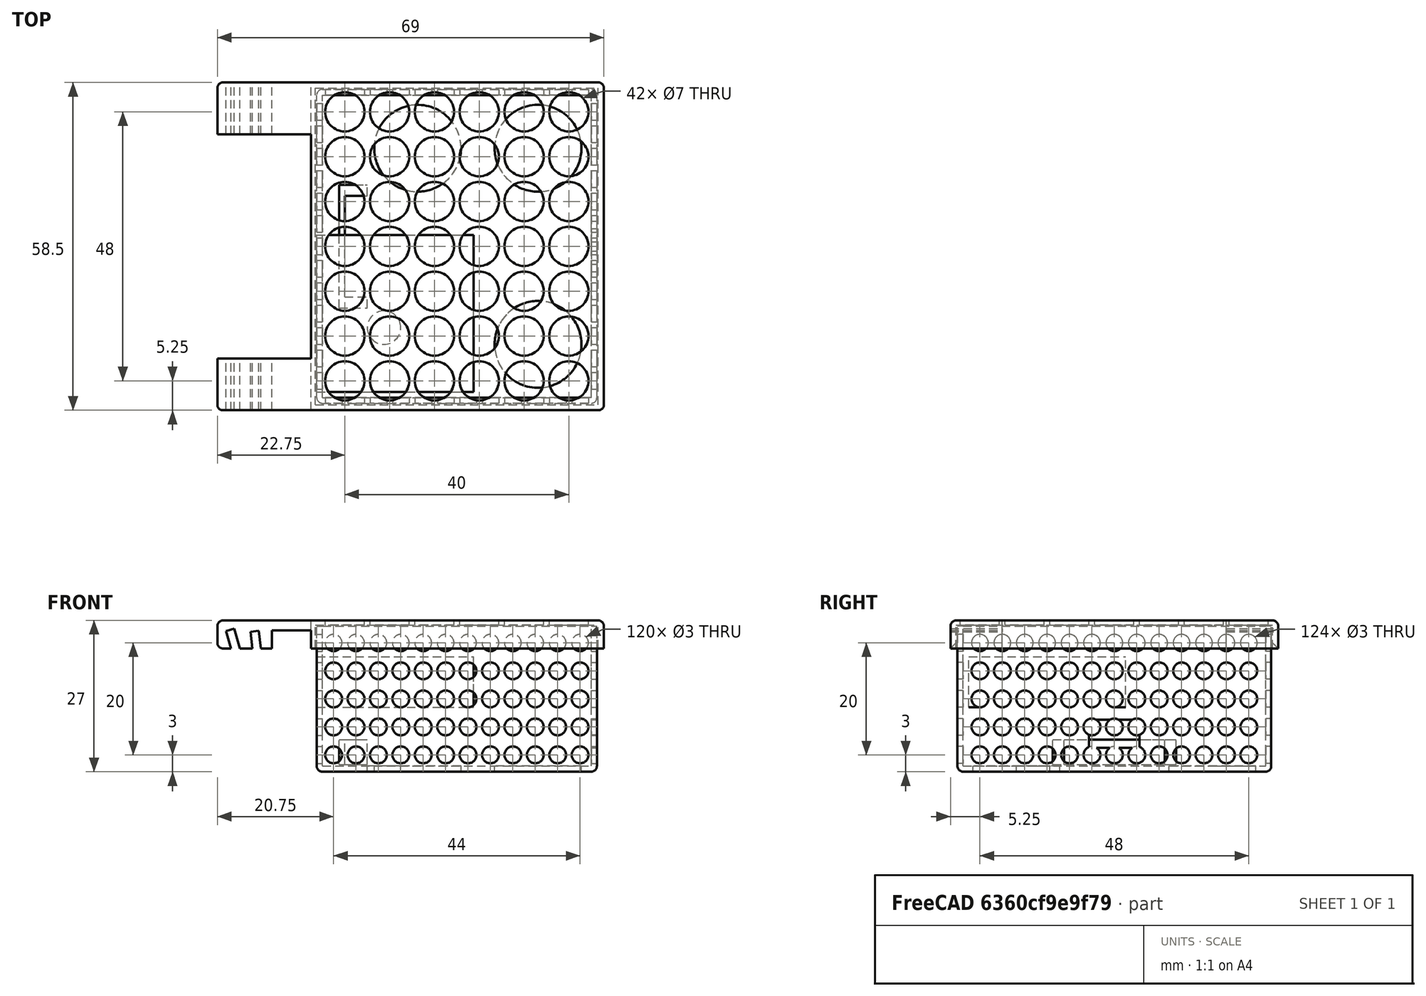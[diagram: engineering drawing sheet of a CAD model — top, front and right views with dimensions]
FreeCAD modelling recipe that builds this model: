
FCSTD DOCUMENT  (FreeCAD 0.16R6703 (Git))
Label: Electronics_BOX_v23
Comment: Muy grande, hay que reducir.. 0,5mm el ancho y largo, \nreducir la base a 0,8mm \naumentar el largo del soporte cortando el 80% desde el centro\naumentar el radio de los agujeros.?
License: CreativeCommons Attribution-ShareAlike
LicenseURL: http://creativecommons.org/licenses/by-sa/4.0/
objects: Part::Box×12, Part::Cut×9, Part::Cylinder×7, Part::MultiFuse×5, Part::FeaturePython×3, Part::Fillet×2
note: 38 computed .brp shape members not serialized (recipe doc carries the construction recipe); baked Part::Feature solids carry a one-line shape summary decoded from their .brp

FEATURE [Part::Box] Box  label="dummy arduino"
  Height = 4.5
  Length = 44
  Placement = pos=(-20,-9,-11.75) rot=(0,0,1;0rad)
  Width = 18
FEATURE [Part::Cylinder] Cylinder  label="Dummy_Button"
  Angle = 360
  Height = 21
  Placement = pos=(14.5,-17.5,-13.5) rot=(0,0,1;0rad)
  Radius = 7.75
FEATURE [Part::Box] Box001  label="dummy RTC"
  Height = 9
  Length = 28
  Placement = pos=(-25,-26,-1.5) rot=(0,0,1;0rad)
  Width = 28
FEATURE [Part::Box] Box002  label="box_int"
  Height = 28
  Length = 48
  Placement = pos=(-24,-27,-12) rot=(0,0,1;0rad)
  Width = 54
FEATURE [Part::Box] Box003  label="box_ext"
  Height = 26
  Length = 50
  Placement = pos=(-25,-28,-13) rot=(0,0,1;0rad)
  Width = 56
FEATURE [Part::Cut] Cut  label="Box"
  Base = -> Box003
  Tool = -> Box002
FEATURE [Part::Box] Box004  label="dummy arduino_usb"
  Height = 5
  Length = 44
  Placement = pos=(-13,-4.5,-8.75) rot=(0,0,1;0rad)
  Width = 9
FEATURE [Part::MultiFuse] Fusion  label="dummy_ardu"
  Shapes = -> [Box,Box004]
FEATURE [Part::Box] Box005  label="soporte_top_arduino"
  Height = 4.5
  Length = 5
  Placement = pos=(-21,-11,-11.75) rot=(0,0,1;0rad)
  Width = 22
FEATURE [Part::Cylinder] Cylinder001  label="Dummy_Button001"
  Angle = 360
  Height = 21
  Placement = pos=(-7,17.5,-13.5) rot=(0,0,1;0rad)
  Radius = 7.75
FEATURE [Part::Cylinder] Cylinder002  label="Dummy_Button002"
  Angle = 360
  Height = 21
  Placement = pos=(14.5,17.5,-13.5) rot=(0,0,1;0rad)
  Radius = 7.75
FEATURE [Part::Cylinder] Cylinder003  label="Hole"
  Angle = 360
  Height = 6
  Placement = pos=(-13,-14.5,-15.5) rot=(0,0,1;0rad)
  Radius = 3
FEATURE [Part::MultiFuse] Fusion001  label="buttons_hole"
  Shapes = -> [Cylinder002,Cylinder001,Cylinder,Cylinder003]
FEATURE [Part::Cylinder] Cylinder004  label="Cylinder"
  Angle = 360
  Height = 90
  Placement = pos=(22,45,10) rot=(1,0,0;1.5708rad)
  Radius = 1.5
FEATURE [Part::FeaturePython] Array  # Draft array (typed FeaturePython)
  Angle = 360
  ArrayType = 0
  Axis = (0,0,1)
  Base = -> Cylinder004
  Center = (0,0,0)
  Fuse = false
  IntervalAxis = (0,0,0)
  IntervalX = (-4,0,0)
  IntervalY = (0,3,0)
  IntervalZ = (0,0,-5)
  NumberPolar = 1
  NumberX = 12
  NumberY = 1
  NumberZ = 5
FEATURE [Part::Cylinder] Cylinder005  label="Cylinder001"
  Angle = 360
  Height = 90
  Placement = pos=(-42,-24,-10) rot=(0,1,0;1.5708rad)
  Radius = 1.5
FEATURE [Part::FeaturePython] Array001  # Draft array (typed FeaturePython)
  Angle = 360
  ArrayType = 0
  Axis = (0,0,1)
  Base = -> Cylinder005
  Center = (0,0,0)
  Fuse = false
  IntervalAxis = (0,0,0)
  IntervalX = (4,0,0)
  IntervalY = (0,4,0)
  IntervalZ = (0,0,5)
  NumberPolar = 1
  NumberX = 1
  NumberY = 13
  NumberZ = 5
FEATURE [Part::MultiFuse] Fusion002  label="holes"
  Shapes = -> [Array,Array001]
FEATURE [Part::Cut] Cut001  label="box_w_holes"
  Base = -> Cut
  Tool = -> Fusion002
FEATURE [Part::MultiFuse] Fusion003
  Shapes = -> [Cut001,Box005]
FEATURE [Part::Cut] Cut002
  Base = -> Fusion003
  Tool = -> Fusion
FEATURE [Part::Cut] Cut003
  Base = -> Cut002
  Tool = -> Fusion001
FEATURE [Part::Fillet] Fillet
  Base = -> Cut003
  Edges = 8 edges r=1: [Edge25,Edge27,Edge28,Edge94,Edge95,Edge163,Edge164,Edge169]
FEATURE [Part::Box] Box006  label="box_int001"
  Height = 4.2
  Length = 50.5
  Placement = pos=(-25.25,-28.25,9) rot=(0,0,1;0rad)
  Width = 56.5
FEATURE [Part::Box] Box007  label="box_ext_001"
  Height = 5
  Length = 69
  Placement = pos=(-42.75,-29.25,9) rot=(0,0,1;0rad)
  Width = 58.5
FEATURE [Part::Cut] Cut004
  Base = -> Box007
  Tool = -> Box006
FEATURE [Part::Box] Box008  label="Cube"
  Height = 72.5
  Length = 1.5
  Placement = pos=(-28,-50,-60) rot=(0,-1,0;0.122173rad)
  Width = 100
FEATURE [Part::Box] Box009  label="Cube001"
  Height = 75
  Length = 1.5
  Placement = pos=(-20.5,-50,-60) rot=(0,-1,0;0.279253rad)
  Width = 100
FEATURE [Part::MultiFuse] Fusion004
  Shapes = -> [Box008,Box009]
FEATURE [Part::Cut] Cut005
  Base = -> Cut004
  Tool = -> Fusion004
FEATURE [Part::Cylinder] Cylinder006  label="Cylinder002"
  Angle = 360
  Height = 8
  Placement = pos=(-20,24,10) rot=(0,0,1;0rad)
  Radius = 3.5
FEATURE [Part::FeaturePython] Array002  # Draft array (typed FeaturePython)
  Angle = 360
  ArrayType = 0
  Axis = (0,0,1)
  Base = -> Cylinder006
  Center = (0,0,0)
  Fuse = false
  IntervalAxis = (0,0,0)
  IntervalX = (8,0,0)
  IntervalY = (0,-8,0)
  IntervalZ = (0,0,0)
  NumberPolar = 1
  NumberX = 6
  NumberY = 7
  NumberZ = 1
FEATURE [Part::Cut] Cut006
  Base = -> Cut005
  Tool = -> Array002
FEATURE [Part::Fillet] Fillet001
  Base = -> Cut006
  Edges = 9 edges r=1: [Edge1,Edge2,Edge3,Edge4,Edge14,Edge15,Edge16,Edge17,Edge69]
FEATURE [Part::Box] Box010  label="Cube002"
  Height = 72.25
  Length = 7
  Placement = pos=(-33,-50,-60) rot=(0,0,1;0rad)
  Width = 100
FEATURE [Part::Cut] Cut007
  Base = -> Fillet001
  Tool = -> Box010
FEATURE [Part::Box] Box011  label="Cube003"
  Height = 40
  Length = 20
  Placement = pos=(-46,-20,-15) rot=(0,0,1;0rad)
  Width = 40
FEATURE [Part::Cut] Cut008
  Base = -> Cut007
  Tool = -> Box011
